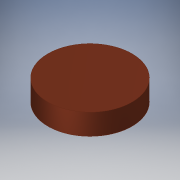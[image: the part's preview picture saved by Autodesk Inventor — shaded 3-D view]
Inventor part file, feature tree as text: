
AUTODESK INVENTOR PART (.ipt)
format: ipt  version: 2018 (Build 220112000, 112)  size: 90,624 bytes
history: native  units: in
note: dims shown in document units (in); Inventor stores cm internally (conversion verified against a paired STEP export)
features: extrude x1, sketch x1
ambient origin geometry x8: Origin, YZ Plane, XZ Plane, XY Plane, X Axis, Y Axis, Z Axis, Center Point
bodies: Solid1 (feature_tree)
feature tree (2):
  extrude  "Extrusion1"  Depth=0.25in TaperAngle=0.0deg
  sketch  "Sketch1"  dims[d0=1.0in d1=0.25in d2=0.0in]
